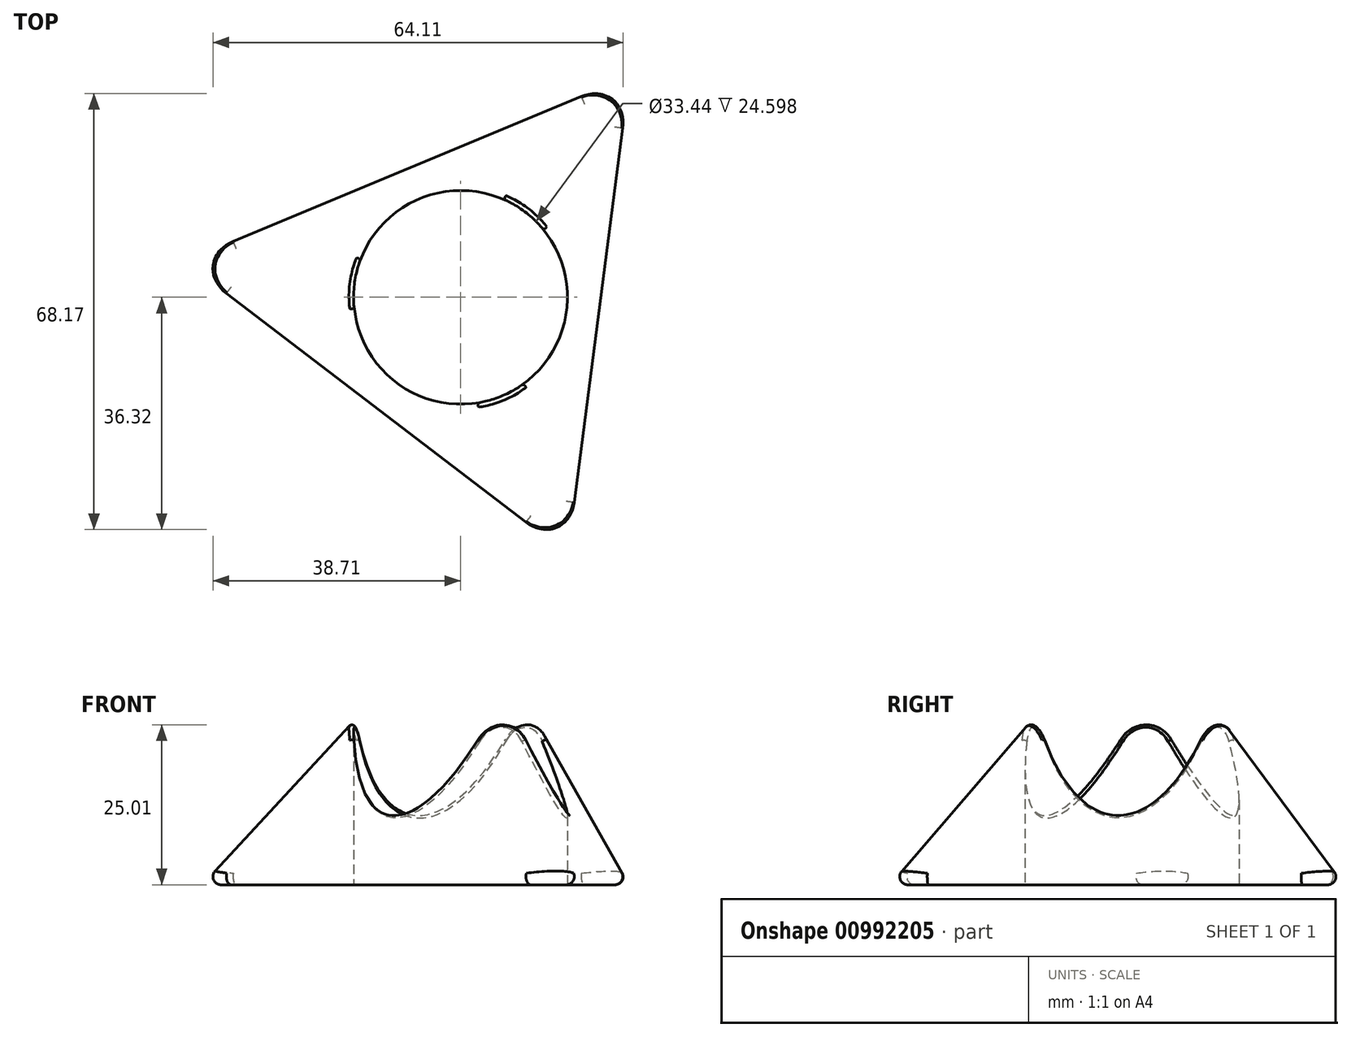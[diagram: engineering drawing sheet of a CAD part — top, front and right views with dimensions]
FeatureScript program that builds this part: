
annotation { "Feature Type Name" : "Feature", "Feature Type Description" : "" }
export const myFeature = defineFeature(function(context is Context, id is Id, definition is map)
    precondition{}
    {
        {
            var Q0;
            Q0=qCreatedBy(makeId("Top.planeOp"),FACE);
            var sketch = newSketch(context, id + "F0", { "sketchPlane" : qUnion([Q0])});
            skCircle(sketch, "E0.cCircle", {"center": v(0, 0) * mm, "radius": 22.46 * mm, "construction": true});
            skLineSegment(sketch, "E0.0", {"start": v(17.27, -41.46) * mm, "end": v(-44.54, 5.78) * mm});
            skLineSegment(sketch, "E0.1", {"start": v(-44.54, 5.78) * mm, "end": v(27.28, 35.69) * mm});
            skLineSegment(sketch, "E0.2", {"start": v(27.28, 35.69) * mm, "end": v(17.27, -41.46) * mm});
            skPoint(sketch, "E0.0.midPoint", {"position": v(-13.64, -17.84) * mm});
            skSolve(sketch);
        }
        {
            var Q0;
            Q0=makeQuery(id+"F0.imprint","IMPRINT",FACE,{"disambiguationData":[TD([[makeQuery(id+"F0.imprint","IMPRINT",EDGE,{"derivedFrom":sQuery(id+"F0.wireOp",EDGE,"E0.0")}),-1.0]])]});
            extrude(context, id + "F1", {"entities" : qUnion([Q0]), "depth" : 51.3 * mm, "offsetDistance" : 25.4 * mm, "hasDraft" : true, "draftAngle" : 25 * degree, "draftPullDirection" : true});
        }
        {
            var Q0;
            Q0=qCreatedBy(makeId("Top.planeOp"),FACE);
            var sketch = newSketch(context, id + "F2", { "sketchPlane" : qUnion([Q0])});
            skCircle(sketch, "E1", {"center": v(0, 0) * mm, "radius": 16.72 * mm});
            skSolve(sketch);
        }
        {
            var Q0;
            Q0=makeQuery(id+"F2.imprint","IMPRINT",FACE,{"disambiguationData":[TD([[makeQuery(id+"F2.imprint","IMPRINT",EDGE,{"derivedFrom":sQuery(id+"F2.wireOp",EDGE,"E1")}),1.0]])]});
            extrude(context, id + "F3", {"entities" : qUnion([Q0]), "operationType" : NewBodyOperationType.REMOVE, "oppositeDirection" : true, "depth" : -254 * mm, "offsetDistance" : 25.4 * mm});
        }
        {
            var Q0;
            Q0=makeQuery(id+"F3.boolean.opBoolean","INTERSECT",EDGE,{"derivedFrom":[makeQuery(id+"F1.opExtrude","SWEPT_FACE",FACE,{"disambiguationData":[OSD([sQuery(id+"F0.wireOp",EDGE,"E0.2")])]}),makeQuery(id+"F3.opExtrude","SWEPT_FACE",FACE,{"disambiguationData":[OSD([sQuery(id+"F2.wireOp",EDGE,"E1")])]})]});
            var Q1;
            Q1=makeQuery(id+"F3.boolean.opBoolean","INTERSECT",EDGE,{"derivedFrom":[makeQuery(id+"F1.opExtrude","SWEPT_FACE",FACE,{"disambiguationData":[OSD([sQuery(id+"F0.wireOp",EDGE,"E0.1")])]}),makeQuery(id+"F3.opExtrude","SWEPT_FACE",FACE,{"disambiguationData":[OSD([sQuery(id+"F2.wireOp",EDGE,"E1")])]})]});
            var Q2;
            Q2=makeQuery(id+"F3.boolean.opBoolean","INTERSECT",EDGE,{"derivedFrom":[makeQuery(id+"F1.opExtrude","SWEPT_FACE",FACE,{"disambiguationData":[OSD([sQuery(id+"F0.wireOp",EDGE,"E0.0")])]}),makeQuery(id+"F3.opExtrude","SWEPT_FACE",FACE,{"disambiguationData":[OSD([sQuery(id+"F2.wireOp",EDGE,"E1")])]})]});
            fillet(context, id + "F4", {"entities" : qUnion([Q0, Q1, Q2]), "radius" : 0.42 * mm, "tangentPropagation" : true, "allowEdgeOverflow" : false});
        }
        {
            var Q0;
            Q0=makeQuery(id+"F1.opExtrude","SWEPT_EDGE",EDGE,{"disambiguationData":[OSD([sQuery(id+"F0.wireOp",EDGE,"E0.1"),sQuery(id+"F0.wireOp",EDGE,"E0.2")])]});
            var Q1;
            Q1=makeQuery(id+"F1.opExtrude","SWEPT_EDGE",EDGE,{"disambiguationData":[OSD([sQuery(id+"F0.wireOp",EDGE,"E0.0"),sQuery(id+"F0.wireOp",EDGE,"E0.1")])]});
            var Q2;
            Q2=makeQuery(id+"F1.opExtrude","SWEPT_EDGE",EDGE,{"disambiguationData":[OSD([sQuery(id+"F0.wireOp",EDGE,"E0.0"),sQuery(id+"F0.wireOp",EDGE,"E0.2")])]});
            fillet(context, id + "F5", {"entities" : qUnion([Q0, Q1, Q2]), "radius" : 5.08 * mm, "tangentPropagation" : true, "allowEdgeOverflow" : false});
        }
        {
            var Q0;
            Q0=makeQuery(id+"F1.opExtrude","CAP_EDGE",EDGE,{"disambiguationData":[OSD([sQuery(id+"F0.wireOp",EDGE,"E0.1")])],"isStart":true});
            fillet(context, id + "F6", {"entities" : qUnion([Q0]), "radius" : 1.27 * mm, "tangentPropagation" : true, "allowEdgeOverflow" : false});
        }
    });
